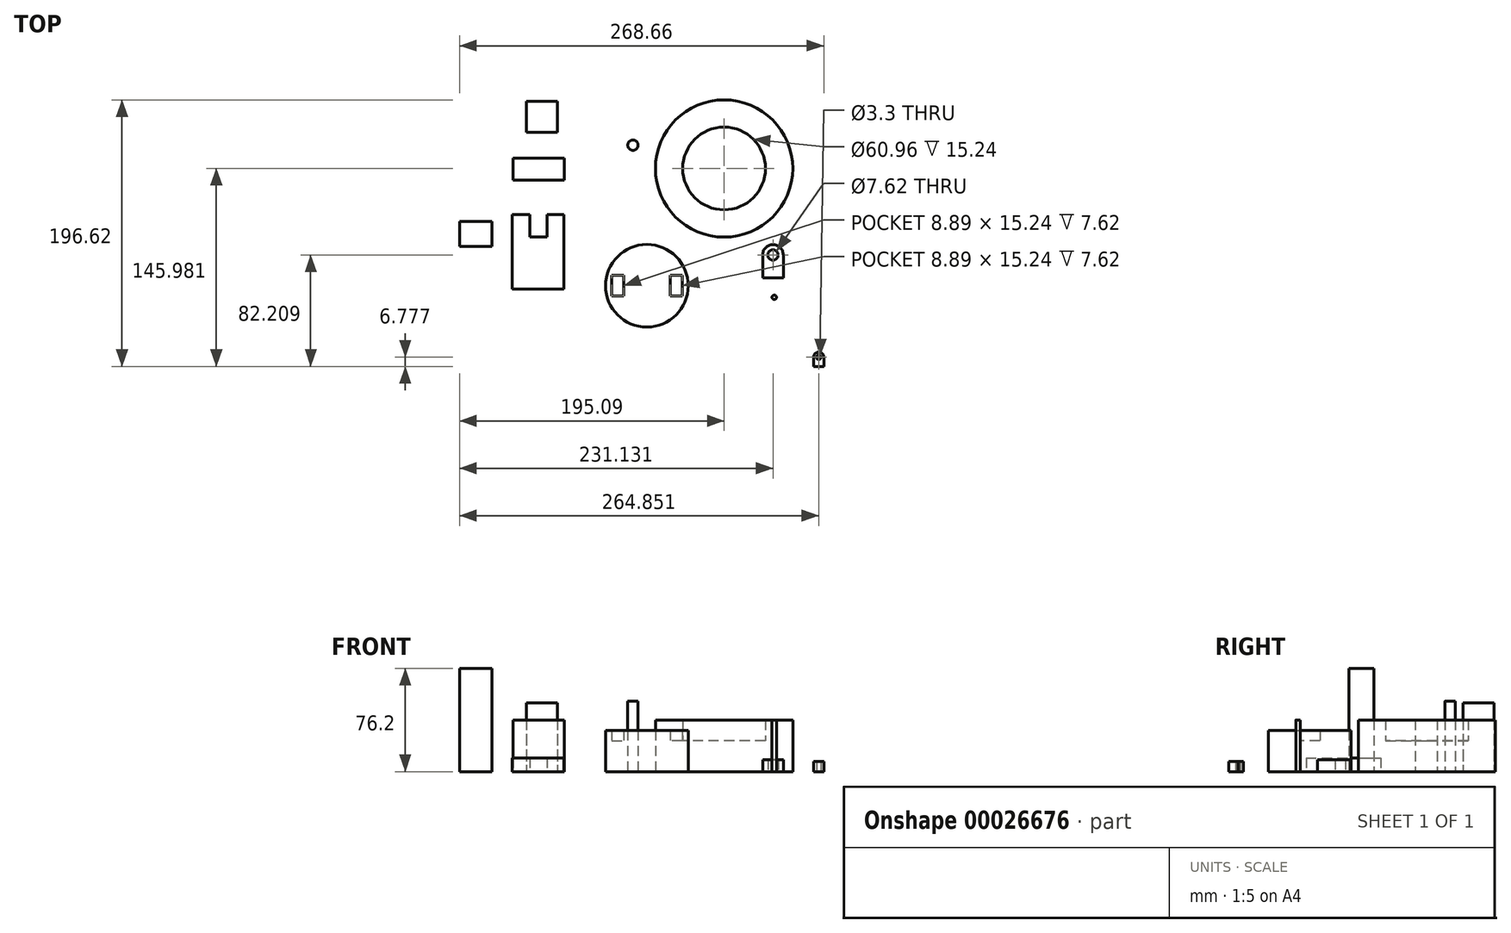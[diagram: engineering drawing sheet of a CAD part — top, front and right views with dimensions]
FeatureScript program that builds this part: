
annotation { "Feature Type Name" : "Feature", "Feature Type Description" : "" }
export const myFeature = defineFeature(function(context is Context, id is Id, definition is map)
    precondition{}
    {
        {
            var Q0;
            Q0=qCreatedBy(makeId("Top.planeOp"),FACE);
            var sketch = newSketch(context, id + "F0", { "sketchPlane" : qUnion([Q0])});
            skCircle(sketch, "E0", {"center": v(0, 30.43) * mm, "radius": 50.64 * mm});
            skCircle(sketch, "E1", {"center": v(0, 30.43) * mm, "radius": 30.48 * mm});
            skSolve(sketch);
        }
        {
            var Q0;
            Q0=makeQuery(id+"F0.imprint","IMPRINT",FACE,{"disambiguationData":[TD([[makeQuery(id+"F0.imprint","IMPRINT",EDGE,{"derivedFrom":sQuery(id+"F0.wireOp",EDGE,"E0")}),1.0]])]});
            extrude(context, id + "F1", {"entities" : qUnion([Q0]), "depth" : 38.1 * mm});
        }
        {
            var Q0;
            Q0=qCreatedBy(makeId("Top.planeOp"),FACE);
            var sketch = newSketch(context, id + "F2", { "sketchPlane" : qUnion([Q0])});
            skCircle(sketch, "E2", {"center": v(0, 25.78) * mm, "radius": 25.93 * mm});
            skSolve(sketch);
        }
        {
            var Q0;
            Q0=makeQuery(id+"F2.imprint","IMPRINT",FACE,{"disambiguationData":[TD([[makeQuery(id+"F2.imprint","IMPRINT",EDGE,{"derivedFrom":sQuery(id+"F2.wireOp",EDGE,"E2")}),1.0]])]});
            extrude(context, id + "F3", {"entities" : qUnion([Q0]), "operationType" : NewBodyOperationType.ADD, "depth" : 22.86 * mm});
        }
        {
            var Q0;
            Q0=makeQuery(id+"F0.imprint","IMPRINT",FACE,{"disambiguationData":[TD([[makeQuery(id+"F0.imprint","IMPRINT",EDGE,{"derivedFrom":sQuery(id+"F0.wireOp",EDGE,"E1")}),1.0]])]});
            extrude(context, id + "F4", {"entities" : qUnion([Q0]), "operationType" : NewBodyOperationType.ADD, "depth" : 22.86 * mm});
        }
        {
            var Q0;
            Q0=qCreatedBy(makeId("Top.planeOp"),FACE);
            var sketch = newSketch(context, id + "F5", { "sketchPlane" : qUnion([Q0])});
            skCircle(sketch, "E3", {"center": v(-56.92, -56.06) * mm, "radius": 30.48 * mm});
            skLineSegment(sketch, "E4", {"start": v(-82.87, -48.44) * mm, "end": v(-82.87, -63.68) * mm});
            skLineSegment(sketch, "E5", {"start": v(-82.87, -48.44) * mm, "end": v(-73.98, -48.44) * mm});
            skLineSegment(sketch, "E6", {"start": v(-73.98, -48.44) * mm, "end": v(-73.98, -63.68) * mm});
            skLineSegment(sketch, "E7", {"start": v(-82.87, -63.68) * mm, "end": v(-73.98, -63.68) * mm});
            skLineSegment(sketch, "E8", {"start": v(-39.69, -48.44) * mm, "end": v(-39.69, -63.68) * mm});
            skLineSegment(sketch, "E9", {"start": v(-39.69, -63.68) * mm, "end": v(-30.8, -63.68) * mm});
            skLineSegment(sketch, "E10", {"start": v(-30.8, -63.68) * mm, "end": v(-30.8, -48.44) * mm});
            skLineSegment(sketch, "E11", {"start": v(-30.8, -48.44) * mm, "end": v(-39.69, -48.44) * mm});
            skLineSegment(sketch, "E12", {"start": v(-73.98, -56.06) * mm, "end": v(-39.69, -56.06) * mm});
            skLineSegment(sketch, "E13", {"start": v(-82.87, -56.06) * mm, "end": v(-30.8, -56.06) * mm});
            skSolve(sketch);
        }
        {
            var Q0;
            Q0 = qSketchRegion(id + "F5", true);
            extrude(context, id + "F6", {"entities" : qUnion([Q0]), "depth" : 30.48 * mm});
        }
        {
            var Q0;
            Q0=qCreatedBy(makeId("Top.planeOp"),FACE);
            var sketch = newSketch(context, id + "F7", { "sketchPlane" : qUnion([Q0])});
            skLineSegment(sketch, "E14", {"start": v(28.42, -33.34) * mm, "end": v(28.42, -50.15) * mm});
            skLineSegment(sketch, "E15", {"start": v(28.42, -50.15) * mm, "end": v(43.66, -50.15) * mm});
            skLineSegment(sketch, "E16", {"start": v(43.66, -50.15) * mm, "end": v(43.66, -33.34) * mm});
            skArc(sketch, "E17", {"start": v(28.42, -33.34) * mm, "mid": v(36.04, -25.72) * mm, "end": v(43.66, -33.34) * mm});
            skCircle(sketch, "E18", {"center": v(36.04, -33.34) * mm, "radius": 3.8 * mm});
            skSolve(sketch);
        }
        {
            var Q0;
            Q0=makeQuery(id+"F7.imprint","IMPRINT",FACE,{"disambiguationData":[TD([[makeQuery(id+"F7.imprint","IMPRINT",EDGE,{"derivedFrom":sQuery(id+"F7.wireOp",EDGE,"E14")}),1.0]])]});
            extrude(context, id + "F8", {"entities" : qUnion([Q0]), "depth" : 8.9 * mm});
        }
        {
            var Q0;
            Q0=qCreatedBy(makeId("Top.planeOp"),FACE);
            var sketch = newSketch(context, id + "F9", { "sketchPlane" : qUnion([Q0])});
            skCircle(sketch, "E19", {"center": v(-67.21, 47.61) * mm, "radius": 3.8 * mm});
            skSolve(sketch);
        }
        {
            var Q0;
            Q0 = qSketchRegion(id + "F9", true);
            extrude(context, id + "F10", {"entities" : qUnion([Q0]), "depth" : 52.07 * mm});
        }
        {
            var Q0;
            Q0=makeQuery(id+"F5.imprint","IMPRINT",FACE,{"disambiguationData":[TD([[makeQuery(id+"F5.imprint","IMPRINT",EDGE,{"derivedFrom":sQuery(id+"F5.wireOp",EDGE,"E4")}),1.0]])]});
            extrude(context, id + "F11", {"entities" : qUnion([Q0]), "operationType" : NewBodyOperationType.ADD, "depth" : 22.86 * mm});
        }
        {
            var Q0;
            Q0=makeQuery(id+"F5.imprint","IMPRINT",FACE,{"disambiguationData":[TD([[makeQuery(id+"F5.imprint","IMPRINT",EDGE,{"derivedFrom":sQuery(id+"F5.wireOp",EDGE,"E8")}),1.0]])]});
            extrude(context, id + "F12", {"entities" : qUnion([Q0]), "operationType" : NewBodyOperationType.ADD, "depth" : 22.86 * mm});
        }
        {
            var Q0;
            Q0=qCreatedBy(makeId("Top.planeOp"),FACE);
            var sketch = newSketch(context, id + "F13", { "sketchPlane" : qUnion([Q0])});
            skLineSegment(sketch, "E20", {"start": v(-145.7, 79.95) * mm, "end": v(-145.7, 57.1) * mm});
            skLineSegment(sketch, "E21", {"start": v(-145.7, 57.1) * mm, "end": v(-122.84, 57.1) * mm});
            skLineSegment(sketch, "E22", {"start": v(-122.84, 57.1) * mm, "end": v(-122.84, 79.95) * mm});
            skLineSegment(sketch, "E23", {"start": v(-145.7, 79.95) * mm, "end": v(-122.84, 79.95) * mm});
            skSolve(sketch);
        }
        {
            var Q0;
            Q0 = qSketchRegion(id + "F13", true);
            extrude(context, id + "F14", {"entities" : qUnion([Q0]), "depth" : 50.8 * mm});
        }
        {
            var Q0;
            Q0=qCreatedBy(makeId("Top.planeOp"),FACE);
            var sketch = newSketch(context, id + "F15", { "sketchPlane" : qUnion([Q0])});
            skLineSegment(sketch, "E24", {"start": v(65.95, -108.77) * mm, "end": v(65.95, -115.55) * mm});
            skLineSegment(sketch, "E25", {"start": v(65.95, -115.55) * mm, "end": v(73.57, -115.55) * mm});
            skLineSegment(sketch, "E26", {"start": v(73.57, -115.55) * mm, "end": v(73.57, -108.63) * mm});
            skArc(sketch, "E27", {"start": v(65.95, -108.77) * mm, "mid": v(69.7, -104.96) * mm, "end": v(73.57, -108.63) * mm});
            skCircle(sketch, "E28", {"center": v(69.76, -108.77) * mm, "radius": 1.65 * mm});
            skSolve(sketch);
        }
        {
            var Q0;
            Q0 = qSketchRegion(id + "F15", true);
            extrude(context, id + "F16", {"entities" : qUnion([Q0]), "depth" : 7.62 * mm});
        }
        {
            var Q0;
            Q0=qCreatedBy(makeId("Top.planeOp"),FACE);
            var sketch = newSketch(context, id + "F17", { "sketchPlane" : qUnion([Q0])});
            skCircle(sketch, "E29", {"center": v(37.01, -64.53) * mm, "radius": 1.64 * mm});
            skSolve(sketch);
        }
        {
            var Q0;
            Q0 = qSketchRegion(id + "F17", true);
            extrude(context, id + "F18", {"entities" : qUnion([Q0]), "depth" : 38.1 * mm});
        }
        {
            var Q0;
            Q0=qCreatedBy(makeId("Top.planeOp"),FACE);
            var sketch = newSketch(context, id + "F19", { "sketchPlane" : qUnion([Q0])});
            skLineSegment(sketch, "E30.bottom", {"start": v(-155.74, 38) * mm, "end": v(-117.64, 38) * mm});
            skLineSegment(sketch, "E30.top", {"start": v(-155.74, 21.73) * mm, "end": v(-117.64, 21.73) * mm});
            skLineSegment(sketch, "E30.left", {"start": v(-155.74, 38) * mm, "end": v(-155.74, 21.73) * mm});
            skLineSegment(sketch, "E30.right", {"start": v(-117.64, 38) * mm, "end": v(-117.64, 21.73) * mm});
            skSolve(sketch);
        }
        {
            var Q0;
            Q0 = qSketchRegion(id + "F19", true);
            extrude(context, id + "F20", {"entities" : qUnion([Q0]), "depth" : 38.1 * mm});
        }
        {
            var Q0;
            Q0=qCreatedBy(makeId("Top.planeOp"),FACE);
            var sketch = newSketch(context, id + "F21", { "sketchPlane" : qUnion([Q0])});
            skLineSegment(sketch, "E31.bottom", {"start": v(-195.09, -8.57) * mm, "end": v(-171.15, -8.57) * mm});
            skLineSegment(sketch, "E31.top", {"start": v(-195.09, -27) * mm, "end": v(-171.15, -27) * mm});
            skLineSegment(sketch, "E31.left", {"start": v(-195.09, -8.57) * mm, "end": v(-195.09, -27) * mm});
            skLineSegment(sketch, "E31.right", {"start": v(-171.15, -8.57) * mm, "end": v(-171.15, -27) * mm});
            skSolve(sketch);
        }
        {
            var Q0;
            Q0=makeQuery(id+"F21.imprint","IMPRINT",FACE,{"disambiguationData":[TD([[makeQuery(id+"F21.imprint","IMPRINT",EDGE,{"derivedFrom":sQuery(id+"F21.wireOp",EDGE,"E31.bottom")}),-1.0]])]});
            extrude(context, id + "F22", {"entities" : qUnion([Q0]), "depth" : 76.2 * mm});
        }
        {
            var Q0;
            Q0=qCreatedBy(makeId("Top.planeOp"),FACE);
            var sketch = newSketch(context, id + "F23", { "sketchPlane" : qUnion([Q0])});
            skLineSegment(sketch, "E32", {"start": v(-156.33, -29.42) * mm, "end": v(-156.33, -3.61) * mm});
            skLineSegment(sketch, "E33", {"start": v(-156.33, -3.61) * mm, "end": v(-143.22, -3.61) * mm});
            skLineSegment(sketch, "E34", {"start": v(-143.22, -3.61) * mm, "end": v(-143.22, -20) * mm});
            skLineSegment(sketch, "E35", {"start": v(-143.22, -20) * mm, "end": v(-130.52, -20) * mm});
            skLineSegment(sketch, "E36", {"start": v(-130.52, -20) * mm, "end": v(-130.52, -3.61) * mm});
            skLineSegment(sketch, "E37", {"start": v(-130.52, -3.61) * mm, "end": v(-118.23, -3.61) * mm});
            skLineSegment(sketch, "E38", {"start": v(-118.23, -3.2) * mm, "end": v(-118.23, -29.42) * mm});
            skLineSegment(sketch, "E39", {"start": v(-156.33, -29.42) * mm, "end": v(-156.33, -58.51) * mm});
            skLineSegment(sketch, "E40", {"start": v(-156.33, -58.51) * mm, "end": v(-118.23, -58.51) * mm});
            skLineSegment(sketch, "E41", {"start": v(-118.23, -58.51) * mm, "end": v(-118.23, -29.42) * mm});
            skSolve(sketch);
        }
        {
            var Q0;
            Q0=makeQuery(id+"F23.imprint","IMPRINT",FACE,{"disambiguationData":[TD([[makeQuery(id+"F23.imprint","IMPRINT",EDGE,{"derivedFrom":sQuery(id+"F23.wireOp",EDGE,"E32")}),-1.0]])]});
            var Q1;
            Q1 = qSketchRegion(id + "F23", true);
            extrude(context, id + "F24", {"entities" : qUnion([Q0, Q1]), "depth" : 10.16 * mm});
        }
    });
